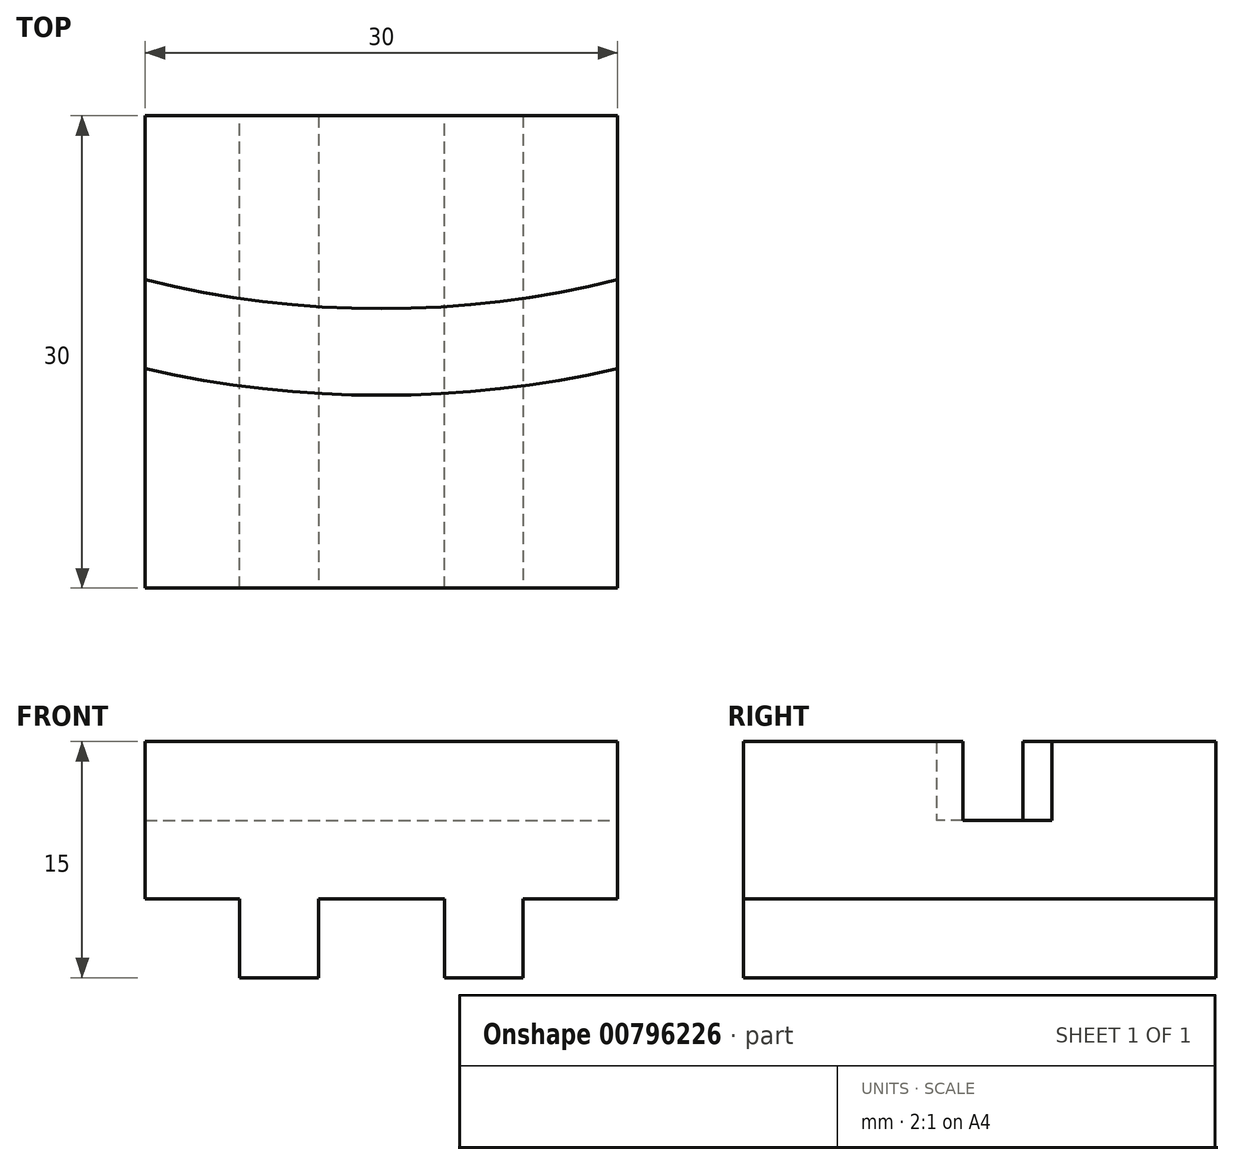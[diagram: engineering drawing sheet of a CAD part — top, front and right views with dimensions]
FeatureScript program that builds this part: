
annotation { "Feature Type Name" : "Feature", "Feature Type Description" : "" }
export const myFeature = defineFeature(function(context is Context, id is Id, definition is map)
    precondition{}
    {
        {
            var Q0;
            Q0=qCreatedBy(makeId("Top.planeOp"),FACE);
            var sketch = newSketch(context, id + "F0", { "sketchPlane" : qUnion([Q0])});
            skLineSegment(sketch, "E0", {"start": v(0, 0) * mm, "end": v(30, 0) * mm});
            skLineSegment(sketch, "E1", {"start": v(30, 0) * mm, "end": v(30, 30) * mm});
            skLineSegment(sketch, "E2", {"start": v(30, 30) * mm, "end": v(0, 30) * mm});
            skLineSegment(sketch, "E3", {"start": v(0, 30) * mm, "end": v(0, 0) * mm});
            skSolve(sketch);
        }
        {
            var Q0;
            Q0 = qSketchRegion(id + "F0", true);
            extrude(context, id + "F1", {"entities" : qUnion([Q0]), "depth" : 5 * mm, "offsetDistance" : 25 * mm});
        }
        {
            var Q0;
            Q0=makeQuery(id+"F1.opExtrude","CAP_FACE",FACE,{"disambiguationData":[OSD([sQuery(id+"F0.wireOp",EDGE,"E0"),sQuery(id+"F0.wireOp",EDGE,"E1"),sQuery(id+"F0.wireOp",EDGE,"E2"),sQuery(id+"F0.wireOp",EDGE,"E3")])],"isStart":false});
            var sketch = newSketch(context, id + "F2", { "sketchPlane" : qUnion([Q0])});
            skCircle(sketch, "E4", {"center": v(15, 80) * mm, "radius": 65 * mm, "construction": true});
            skPoint(sketch, "E4.centerSnap0", {"position": v(15, 30) * mm});
            skCircle(sketch, "E5", {"center": v(15, 80) * mm, "radius": 67.75 * mm, "construction": true});
            skCircle(sketch, "E6", {"center": v(15, 80) * mm, "radius": 62.25 * mm, "construction": true});
            skLineSegment(sketch, "E7", {"start": v(0, 19.58) * mm, "end": v(0, 30) * mm});
            skLineSegment(sketch, "E8", {"start": v(0, 30) * mm, "end": v(30, 30) * mm});
            skLineSegment(sketch, "E9", {"start": v(30, 30) * mm, "end": v(30, 19.58) * mm});
            skLineSegment(sketch, "E10", {"start": v(30, 13.93) * mm, "end": v(30, 0) * mm});
            skLineSegment(sketch, "E11", {"start": v(30, 0) * mm, "end": v(0, 0) * mm});
            skLineSegment(sketch, "E12", {"start": v(0, 0) * mm, "end": v(0, 13.93) * mm});
            skArc(sketch, "E13", {"start": v(30, 19.58) * mm, "mid": v(15, 17.75) * mm, "end": v(0, 19.58) * mm});
            skArc(sketch, "E14", {"start": v(30, 13.93) * mm, "mid": v(15, 12.25) * mm, "end": v(0, 13.93) * mm});
            skSolve(sketch);
        }
        {
            var Q0;
            Q0 = qSketchRegion(id + "F2", true);
            extrude(context, id + "F3", {"entities" : qUnion([Q0]), "operationType" : NewBodyOperationType.ADD, "depth" : 5 * mm, "offsetDistance" : 25 * mm});
        }
        {
            var Q0;
            Q0=makeQuery(id+"F1.opExtrude","CAP_FACE",FACE,{"disambiguationData":[OSD([sQuery(id+"F0.wireOp",EDGE,"E0"),sQuery(id+"F0.wireOp",EDGE,"E1"),sQuery(id+"F0.wireOp",EDGE,"E2"),sQuery(id+"F0.wireOp",EDGE,"E3")])],"isStart":true});
            var sketch = newSketch(context, id + "F4", { "sketchPlane" : qUnion([Q0])});
            skLineSegment(sketch, "E15", {"start": v(6, 0) * mm, "end": v(6, -30) * mm});
            skLineSegment(sketch, "E16", {"start": v(6, -30) * mm, "end": v(11, -30) * mm});
            skLineSegment(sketch, "E17", {"start": v(11, -30) * mm, "end": v(11, 0) * mm});
            skLineSegment(sketch, "E18", {"start": v(11, 0) * mm, "end": v(6, 0) * mm});
            skLineSegment(sketch, "E19", {"start": v(19, 0) * mm, "end": v(19, -30) * mm});
            skLineSegment(sketch, "E20", {"start": v(19, -30) * mm, "end": v(24, -30) * mm});
            skLineSegment(sketch, "E21", {"start": v(24, -30) * mm, "end": v(24, 0) * mm});
            skLineSegment(sketch, "E22", {"start": v(24, 0) * mm, "end": v(19, 0) * mm});
            skSolve(sketch);
        }
        {
            var Q0;
            Q0 = qSketchRegion(id + "F4", true);
            extrude(context, id + "F5", {"entities" : qUnion([Q0]), "operationType" : NewBodyOperationType.ADD, "depth" : 5 * mm, "offsetDistance" : 25 * mm});
        }
    });
